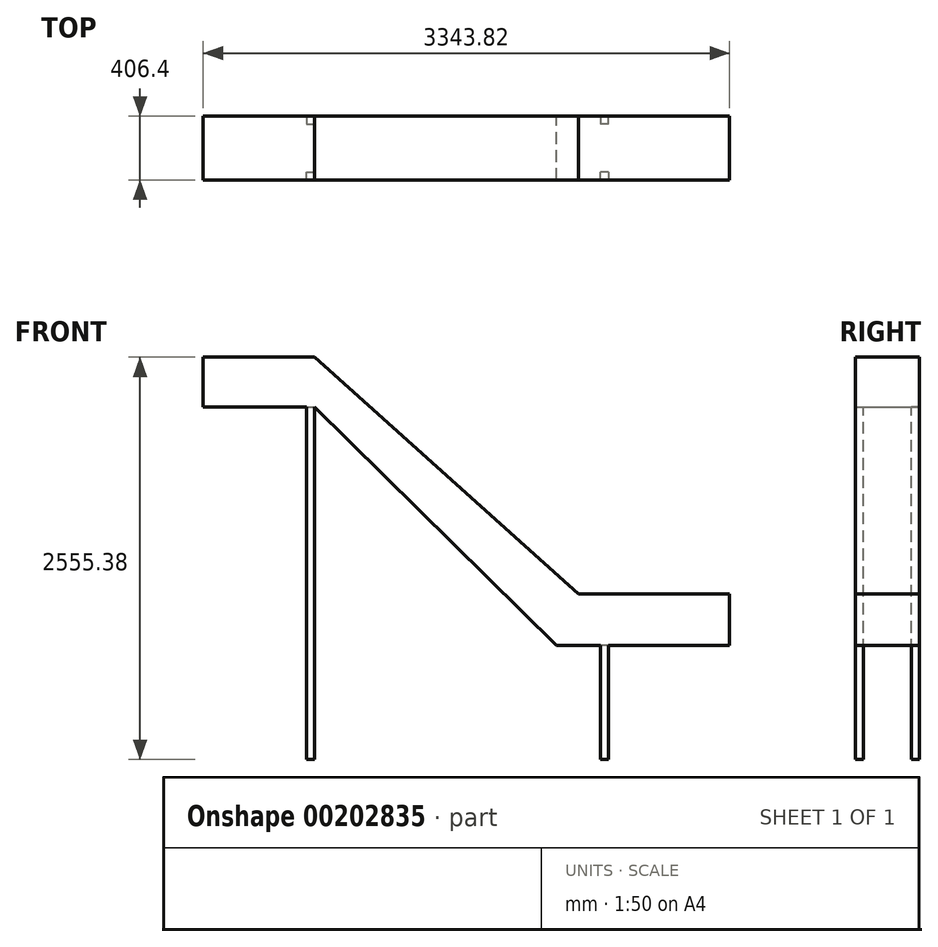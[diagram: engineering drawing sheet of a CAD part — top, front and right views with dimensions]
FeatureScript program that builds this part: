
annotation { "Feature Type Name" : "Feature", "Feature Type Description" : "" }
export const myFeature = defineFeature(function(context is Context, id is Id, definition is map)
    precondition{}
    {
        {
            var Q0;
            Q0=qCreatedBy(makeId("Front.planeOp"),FACE);
            var sketch = newSketch(context, id + "F0", { "sketchPlane" : qUnion([Q0])});
            skLineSegment(sketch, "E0", {"start": v(-64.63, 66.36) * mm, "end": v(-64.63, -250.87) * mm});
            skLineSegment(sketch, "E1", {"start": v(-64.63, -250.87) * mm, "end": v(644.48, -250.87) * mm});
            skLineSegment(sketch, "E2", {"start": v(-64.63, 66.36) * mm, "end": v(644.48, 66.36) * mm});
            skLineSegment(sketch, "E3", {"start": v(644.48, 66.36) * mm, "end": v(2319.05, -1437.91) * mm});
            skLineSegment(sketch, "E4", {"start": v(2319.05, -1437.91) * mm, "end": v(3279.19, -1437.91) * mm});
            skLineSegment(sketch, "E5", {"start": v(3279.19, -1437.91) * mm, "end": v(3279.19, -1764.88) * mm});
            skLineSegment(sketch, "E6", {"start": v(3279.19, -1764.88) * mm, "end": v(2178.92, -1764.88) * mm});
            skLineSegment(sketch, "E7", {"start": v(2178.92, -1764.88) * mm, "end": v(644.48, -250.87) * mm});
            skSolve(sketch);
        }
        {
            var Q0;
            Q0 = qSketchRegion(id + "F0", true);
            extrude(context, id + "F1", {"entities" : qUnion([Q0]), "endBound" : BoundingType.SYMMETRIC, "depth" : 406.4 * mm});
        }
        {
            var Q0;
            Q0=makeQuery(id+"F1.opExtrude","CAP_FACE",FACE,{"disambiguationData":[OSD([sQuery(id+"F0.wireOp",EDGE,"E0"),sQuery(id+"F0.wireOp",EDGE,"E1"),sQuery(id+"F0.wireOp",EDGE,"E2"),sQuery(id+"F0.wireOp",EDGE,"E3"),sQuery(id+"F0.wireOp",EDGE,"E4"),sQuery(id+"F0.wireOp",EDGE,"E5"),sQuery(id+"F0.wireOp",EDGE,"E6"),sQuery(id+"F0.wireOp",EDGE,"E7")])],"isStart":false});
            var sketch = newSketch(context, id + "F2", { "sketchPlane" : qUnion([Q0])});
            skLineSegment(sketch, "E8", {"start": v(644.48, 66.36) * mm, "end": v(644.48, -2489.02) * mm});
            skLineSegment(sketch, "E9", {"start": v(644.48, -2489.02) * mm, "end": v(593.68, -2489.02) * mm});
            skLineSegment(sketch, "E10", {"start": v(593.68, -2489.02) * mm, "end": v(593.68, 66.36) * mm});
            skLineSegment(sketch, "E11", {"start": v(593.68, 66.36) * mm, "end": v(644.48, 66.36) * mm});
            skLineSegment(sketch, "E12", {"start": v(2460.31, -1437.91) * mm, "end": v(2460.31, -2489.02) * mm});
            skLineSegment(sketch, "E13", {"start": v(2460.31, -2489.02) * mm, "end": v(2511.11, -2489.02) * mm});
            skLineSegment(sketch, "E14", {"start": v(2511.11, -2489.02) * mm, "end": v(2511.11, -1437.91) * mm});
            skLineSegment(sketch, "E15", {"start": v(2511.11, -1437.91) * mm, "end": v(2460.31, -1437.91) * mm});
            skSolve(sketch);
        }
        {
            var Q0;
            Q0 = qSketchRegion(id + "F2", true);
            extrude(context, id + "F3", {"entities" : qUnion([Q0]), "operationType" : NewBodyOperationType.ADD, "oppositeDirection" : true, "depth" : 50.8 * mm});
        }
        {
            var Q0;
            Q0=makeQuery(id+"F1.opExtrude","SWEPT_BODY",BODY,{"disambiguationData":[OSD([sQuery(id+"F0.wireOp",EDGE,"E0"),sQuery(id+"F0.wireOp",EDGE,"E1"),sQuery(id+"F0.wireOp",EDGE,"E2"),sQuery(id+"F0.wireOp",EDGE,"E3"),sQuery(id+"F0.wireOp",EDGE,"E4"),sQuery(id+"F0.wireOp",EDGE,"E5"),sQuery(id+"F0.wireOp",EDGE,"E6"),sQuery(id+"F0.wireOp",EDGE,"E7")])]});
            var Q1;
            Q1=qCreatedBy(makeId("Front.planeOp"),FACE);
            mirror(context, id + "F4", {"operationType" : NewBodyOperationType.ADD, "entities" : qUnion([Q0]), "mirrorPlane" : qUnion([Q1])});
        }
    });
